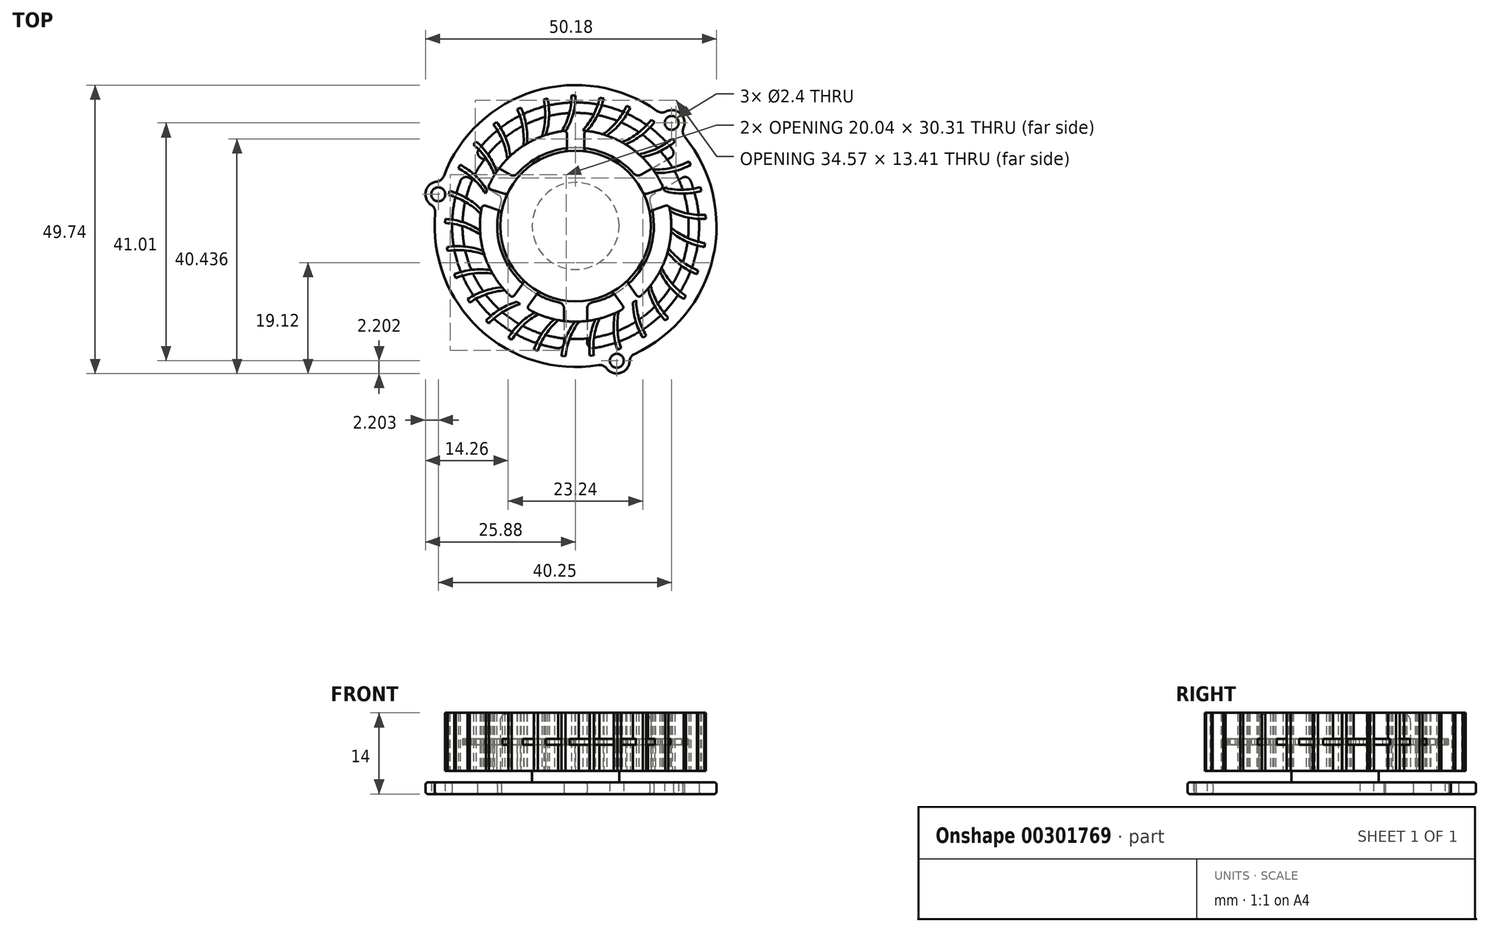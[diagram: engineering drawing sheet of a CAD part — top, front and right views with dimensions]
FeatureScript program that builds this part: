
annotation { "Feature Type Name" : "Feature", "Feature Type Description" : "" }
export const myFeature = defineFeature(function(context is Context, id is Id, definition is map)
    precondition{}
    {
        {
            var Q0;
            Q0=qCreatedBy(makeId("Top.planeOp"),FACE);
            var sketch = newSketch(context, id + "F0", { "sketchPlane" : qUnion([Q0])});
            skArc(sketch, "E0", {"start": v(-24.2, 2.23) * mm, "mid": v(-16.57, -17.77) * mm, "end": v(3.9, -23.98) * mm});
            skLineSegment(sketch, "E1", {"start": v(0, 0) * mm, "end": v(-18.45, 10.65) * mm, "construction": true});
            skLineSegment(sketch, "E2", {"start": v(18.45, 10.65) * mm, "end": v(0, 0) * mm, "construction": true});
            skLineSegment(sketch, "E3", {"start": v(0, 0) * mm, "end": v(0, -21.3) * mm, "construction": true});
            skLineSegment(sketch, "E4", {"start": v(-16.39, 11.77) * mm, "end": v(-11.29, 8.83) * mm});
            skLineSegment(sketch, "E5", {"start": v(11.29, 8.83) * mm, "end": v(16.39, 11.77) * mm});
            skLineSegment(sketch, "E6", {"start": v(-18.39, 8.3) * mm, "end": v(-13.29, 5.36) * mm});
            skLineSegment(sketch, "E7", {"start": v(-2, -14.19) * mm, "end": v(-2, -20.08) * mm});
            skLineSegment(sketch, "E8", {"start": v(18.39, 8.3) * mm, "end": v(13.29, 5.36) * mm});
            skLineSegment(sketch, "E9", {"start": v(2, -14.19) * mm, "end": v(2, -20.08) * mm});
            skCircle(sketch, "E10", {"center": v(0, 0) * mm, "radius": 2 * mm, "construction": true});
            skArc(sketch, "E11", {"start": v(-16.67, 13.26) * mm, "mid": v(-16.87, 12.45) * mm, "end": v(-16.39, 11.77) * mm});
            skArc(sketch, "E12", {"start": v(16.39, 11.77) * mm, "mid": v(16.87, 12.45) * mm, "end": v(16.67, 13.26) * mm});
            skArc(sketch, "E13", {"start": v(19.82, 7.8) * mm, "mid": v(19.22, 8.38) * mm, "end": v(18.39, 8.3) * mm});
            skArc(sketch, "E14", {"start": v(2, -20.08) * mm, "mid": v(2.35, -20.83) * mm, "end": v(3.15, -21.07) * mm});
            skArc(sketch, "E15", {"start": v(-3.15, -21.07) * mm, "mid": v(-2.35, -20.83) * mm, "end": v(-2, -20.08) * mm});
            skArc(sketch, "E16", {"start": v(-18.39, 8.3) * mm, "mid": v(-19.22, 8.38) * mm, "end": v(-19.82, 7.8) * mm});
            skArc(sketch, "E17.trimOffspring", {"start": v(-19.82, 7.8) * mm, "mid": v(-18.45, -10.65) * mm, "end": v(-3.15, -21.07) * mm});
            skArc(sketch, "E18.trimOffspring", {"start": v(3.15, -21.07) * mm, "mid": v(18.45, -10.65) * mm, "end": v(19.82, 7.8) * mm});
            skArc(sketch, "E19.trimOffspring", {"start": v(16.67, 13.26) * mm, "mid": v(0, 21.3) * mm, "end": v(-16.67, 13.26) * mm});
            skCircle(sketch, "E20", {"center": v(-23.68, 5.47) * mm, "radius": 1.2 * mm});
            skCircle(sketch, "E21", {"center": v(16.57, 17.77) * mm, "radius": 1.2 * mm});
            skCircle(sketch, "E22", {"center": v(7.1, -23.24) * mm, "radius": 1.2 * mm});
            skCircle(sketch, "E23", {"center": v(0, 0) * mm, "radius": 23.1 * mm, "construction": true});
            skArc(sketch, "E24", {"start": v(18.6, 16.91) * mm, "mid": v(18.07, 19.38) * mm, "end": v(15.57, 19.73) * mm});
            skArc(sketch, "E25", {"start": v(-23.94, 7.65) * mm, "mid": v(-25.82, 5.96) * mm, "end": v(-24.87, 3.62) * mm});
            skArc(sketch, "E26", {"start": v(5.35, -24.56) * mm, "mid": v(7.75, -25.34) * mm, "end": v(9.3, -23.35) * mm});
            skArc(sketch, "E27.trimOffspring", {"start": v(10.17, -22.07) * mm, "mid": v(23.68, -5.47) * mm, "end": v(18.82, 15.38) * mm});
            skArc(sketch, "E28.trimOffspring", {"start": v(14.03, 19.84) * mm, "mid": v(-7.1, 23.24) * mm, "end": v(-22.72, 8.6) * mm});
            skArc(sketch, "E29.filletArc", {"start": v(14.03, 19.84) * mm, "mid": v(14.78, 19.57) * mm, "end": v(15.57, 19.73) * mm});
            skArc(sketch, "E30.filletArc", {"start": v(18.6, 16.91) * mm, "mid": v(18.5, 16.11) * mm, "end": v(18.82, 15.38) * mm});
            skArc(sketch, "E31.filletArc", {"start": v(10.17, -22.07) * mm, "mid": v(9.56, -22.59) * mm, "end": v(9.3, -23.35) * mm});
            skArc(sketch, "E32.filletArc", {"start": v(5.35, -24.56) * mm, "mid": v(4.7, -24.07) * mm, "end": v(3.9, -23.98) * mm});
            skArc(sketch, "E33.filletArc", {"start": v(-24.2, 2.23) * mm, "mid": v(-24.34, 3.02) * mm, "end": v(-24.87, 3.62) * mm});
            skArc(sketch, "E34.filletArc", {"start": v(-23.94, 7.65) * mm, "mid": v(-23.2, 7.96) * mm, "end": v(-22.72, 8.6) * mm});
            skLineSegment(sketch, "E35", {"start": v(-23.68, 5.47) * mm, "end": v(0, 0) * mm, "construction": true});
            skLineSegment(sketch, "E36", {"start": v(0, 0) * mm, "end": v(16.57, 17.77) * mm, "construction": true});
            skArc(sketch, "E37", {"start": v(-12.83, 4.19) * mm, "mid": v(-11.7, -6.75) * mm, "end": v(-2.8, -13.2) * mm});
            skLineSegment(sketch, "E38.trimOffspring", {"start": v(0, 0) * mm, "end": v(7.1, -23.24) * mm, "construction": true});
            skArc(sketch, "E39.trimOffspring", {"start": v(10.04, 9.02) * mm, "mid": v(0, 13.5) * mm, "end": v(-10.04, 9.02) * mm});
            skArc(sketch, "E40.trimOffspring", {"start": v(2.8, -13.2) * mm, "mid": v(11.7, -6.75) * mm, "end": v(12.83, 4.19) * mm});
            skArc(sketch, "E41.filletArc", {"start": v(-11.29, 8.83) * mm, "mid": v(-10.63, 8.7) * mm, "end": v(-10.04, 9.02) * mm});
            skArc(sketch, "E42.filletArc", {"start": v(10.04, 9.02) * mm, "mid": v(10.63, 8.7) * mm, "end": v(11.29, 8.83) * mm});
            skArc(sketch, "E43.filletArc", {"start": v(13.29, 5.36) * mm, "mid": v(12.85, 4.85) * mm, "end": v(12.83, 4.19) * mm});
            skArc(sketch, "E44.filletArc", {"start": v(2.8, -13.2) * mm, "mid": v(2.22, -13.56) * mm, "end": v(2, -14.19) * mm});
            skArc(sketch, "E45.filletArc", {"start": v(-2, -14.19) * mm, "mid": v(-2.22, -13.56) * mm, "end": v(-2.8, -13.2) * mm});
            skArc(sketch, "E46.filletArc", {"start": v(-12.83, 4.19) * mm, "mid": v(-12.85, 4.85) * mm, "end": v(-13.29, 5.36) * mm});
            skCircle(sketch, "E47", {"center": v(0, 0) * mm, "radius": 7.5 * mm});
            skSolve(sketch);
        }
        {
            var Q0;
            Q0=makeQuery(id+"F0.imprint","IMPRINT",FACE,{"disambiguationData":[TD([[makeQuery(id+"F0.imprint","IMPRINT",EDGE,{"derivedFrom":sQuery(id+"F0.wireOp",EDGE,"E0")}),1.0]])]});
            var Q1;
            Q1=makeQuery(id+"F0.imprint","IMPRINT",FACE,{"disambiguationData":[TD([[makeQuery(id+"F0.imprint","IMPRINT",EDGE,{"derivedFrom":sQuery(id+"F0.wireOp",EDGE,"E47")}),1.0]])]});
            extrude(context, id + "F1", {"entities" : qUnion([Q0, Q1]), "depth" : 2 * mm});
        }
        {
            var Q0;
            Q0=makeQuery(id+"F1.opExtrude","CAP_EDGE",EDGE,{"disambiguationData":[OSD([sQuery(id+"F0.wireOp",EDGE,"E28.trimOffspring")])],"isStart":true});
            var Q1;
            Q1=makeQuery(id+"F1.opExtrude","CAP_EDGE",EDGE,{"disambiguationData":[OSD([sQuery(id+"F0.wireOp",EDGE,"E28.trimOffspring")])],"isStart":false});
            var Q2;
            Q2=makeQuery(id+"F1.opExtrude","CAP_EDGE",EDGE,{"disambiguationData":[OSD([sQuery(id+"F0.wireOp",EDGE,"E39.trimOffspring")])],"isStart":true});
            var Q3;
            Q3=makeQuery(id+"F1.opExtrude","CAP_EDGE",EDGE,{"disambiguationData":[OSD([sQuery(id+"F0.wireOp",EDGE,"E39.trimOffspring")])],"isStart":false});
            var Q4;
            Q4=makeQuery(id+"F1.opExtrude","CAP_EDGE",EDGE,{"disambiguationData":[OSD([sQuery(id+"F0.wireOp",EDGE,"E37")])],"isStart":true});
            var Q5;
            Q5=makeQuery(id+"F1.opExtrude","CAP_EDGE",EDGE,{"disambiguationData":[OSD([sQuery(id+"F0.wireOp",EDGE,"E37")])],"isStart":false});
            var Q6;
            Q6=makeQuery(id+"F1.opExtrude","CAP_EDGE",EDGE,{"disambiguationData":[OSD([sQuery(id+"F0.wireOp",EDGE,"E40.trimOffspring")])],"isStart":false});
            var Q7;
            Q7=makeQuery(id+"F1.opExtrude","CAP_EDGE",EDGE,{"disambiguationData":[OSD([sQuery(id+"F0.wireOp",EDGE,"E18.trimOffspring")])],"isStart":true});
            fillet(context, id + "F2", {"entities" : qUnion([Q0, Q1, Q2, Q3, Q4, Q5, Q6, Q7]), "radius" : 0.4 * mm, "tangentPropagation" : true, "allowEdgeOverflow" : false});
        }
        {
            var Q0;
            Q0=makeQuery(id+"F0.imprint","IMPRINT",FACE,{"disambiguationData":[TD([[makeQuery(id+"F0.imprint","IMPRINT",EDGE,{"derivedFrom":sQuery(id+"F0.wireOp",EDGE,"E47")}),1.0]])]});
            extrude(context, id + "F3", {"entities" : qUnion([Q0]), "operationType" : NewBodyOperationType.ADD, "depth" : 4 * mm});
        }
        {
            var Q0;
            Q0=makeQuery(id+"F3.opExtrude","CAP_FACE",FACE,{"disambiguationData":[OSD([sQuery(id+"F0.wireOp",EDGE,"E47")])],"isStart":false});
            var sketch = newSketch(context, id + "F4", { "sketchPlane" : qUnion([Q0])});
            skCircle(sketch, "E48", {"center": v(0, 0) * mm, "radius": 22.5 * mm, "construction": true});
            skCircle(sketch, "E49", {"center": v(0, 0) * mm, "radius": 19.5 * mm});
            skArc(sketch, "E50", {"start": v(-2.06, 16.37) * mm, "mid": v(-9.7, 13.35) * mm, "end": v(-14.93, 7.02) * mm});
            skArc(sketch, "E51", {"start": v(-1.93, 12.86) * mm, "mid": v(-7.64, 10.52) * mm, "end": v(-11.63, 5.8) * mm});
            skLineSegment(sketch, "E52", {"start": v(0, 13) * mm, "end": v(0, 16.5) * mm, "construction": true});
            skLineSegment(sketch, "E53", {"start": v(-1.5, 15.87) * mm, "end": v(-1.5, 13.35) * mm});
            skLineSegment(sketch, "E54", {"start": v(1.5, 15.87) * mm, "end": v(1.5, 13.35) * mm});
            skArc(sketch, "E55", {"start": v(-1.5, 15.87) * mm, "mid": v(-1.67, 16.25) * mm, "end": v(-2.06, 16.37) * mm});
            skArc(sketch, "E56", {"start": v(-1.93, 12.86) * mm, "mid": v(-1.62, 13.02) * mm, "end": v(-1.5, 13.35) * mm});
            skArc(sketch, "E57", {"start": v(1.5, 13.35) * mm, "mid": v(1.62, 13.02) * mm, "end": v(1.93, 12.86) * mm});
            skArc(sketch, "E58", {"start": v(2.06, 16.37) * mm, "mid": v(1.67, 16.25) * mm, "end": v(1.5, 15.87) * mm});
            skLineSegment(sketch, "E59.1.0", {"start": v(-12.36, 4.02) * mm, "end": v(-15.7, 5.1) * mm, "construction": true});
            skLineSegment(sketch, "E59.1.1", {"start": v(-14.63, 6.33) * mm, "end": v(-12.23, 5.55) * mm});
            skLineSegment(sketch, "E59.1.2", {"start": v(-15.56, 3.48) * mm, "end": v(-13.16, 2.7) * mm});
            skArc(sketch, "E59.1.3", {"start": v(-15.56, 3.48) * mm, "mid": v(-15.97, 3.43) * mm, "end": v(-16.2, 3.1) * mm});
            skArc(sketch, "E59.1.4", {"start": v(-12.82, 2.14) * mm, "mid": v(-12.89, 2.48) * mm, "end": v(-13.16, 2.7) * mm});
            skArc(sketch, "E59.1.5", {"start": v(-12.23, 5.55) * mm, "mid": v(-11.89, 5.57) * mm, "end": v(-11.63, 5.8) * mm});
            skArc(sketch, "E59.1.6", {"start": v(-14.93, 7.02) * mm, "mid": v(-14.94, 6.6) * mm, "end": v(-14.63, 6.33) * mm});
            skLineSegment(sketch, "E59.2.0", {"start": v(-7.64, -10.52) * mm, "end": v(-9.7, -13.35) * mm, "construction": true});
            skLineSegment(sketch, "E59.2.1", {"start": v(-10.54, -11.96) * mm, "end": v(-9.06, -9.92) * mm});
            skLineSegment(sketch, "E59.2.2", {"start": v(-8.12, -13.72) * mm, "end": v(-6.63, -11.68) * mm});
            skArc(sketch, "E59.2.3", {"start": v(-8.12, -13.72) * mm, "mid": v(-8.2, -14.13) * mm, "end": v(-7.95, -14.46) * mm});
            skArc(sketch, "E59.2.4", {"start": v(-6, -11.53) * mm, "mid": v(-6.34, -11.5) * mm, "end": v(-6.63, -11.68) * mm});
            skArc(sketch, "E59.2.5", {"start": v(-9.06, -9.92) * mm, "mid": v(-8.97, -9.58) * mm, "end": v(-9.11, -9.27) * mm});
            skArc(sketch, "E59.2.6", {"start": v(-11.3, -12.03) * mm, "mid": v(-10.9, -12.16) * mm, "end": v(-10.54, -11.96) * mm});
            skLineSegment(sketch, "E59.3.0", {"start": v(7.64, -10.52) * mm, "end": v(9.7, -13.35) * mm, "construction": true});
            skLineSegment(sketch, "E59.3.1", {"start": v(8.12, -13.72) * mm, "end": v(6.63, -11.68) * mm});
            skLineSegment(sketch, "E59.3.2", {"start": v(10.54, -11.96) * mm, "end": v(9.06, -9.92) * mm});
            skArc(sketch, "E59.3.3", {"start": v(10.54, -11.96) * mm, "mid": v(10.9, -12.16) * mm, "end": v(11.3, -12.03) * mm});
            skArc(sketch, "E59.3.4", {"start": v(9.11, -9.27) * mm, "mid": v(8.97, -9.58) * mm, "end": v(9.06, -9.92) * mm});
            skArc(sketch, "E59.3.5", {"start": v(6.63, -11.68) * mm, "mid": v(6.34, -11.5) * mm, "end": v(6, -11.53) * mm});
            skArc(sketch, "E59.3.6", {"start": v(7.95, -14.46) * mm, "mid": v(8.2, -14.13) * mm, "end": v(8.12, -13.72) * mm});
            skLineSegment(sketch, "E59.4.0", {"start": v(12.36, 4.02) * mm, "end": v(15.7, 5.1) * mm, "construction": true});
            skLineSegment(sketch, "E59.4.1", {"start": v(15.56, 3.48) * mm, "end": v(13.16, 2.7) * mm});
            skLineSegment(sketch, "E59.4.2", {"start": v(14.63, 6.33) * mm, "end": v(12.23, 5.55) * mm});
            skArc(sketch, "E59.4.3", {"start": v(14.63, 6.33) * mm, "mid": v(14.94, 6.6) * mm, "end": v(14.93, 7.02) * mm});
            skArc(sketch, "E59.4.4", {"start": v(11.63, 5.8) * mm, "mid": v(11.89, 5.57) * mm, "end": v(12.23, 5.55) * mm});
            skArc(sketch, "E59.4.5", {"start": v(13.16, 2.7) * mm, "mid": v(12.89, 2.48) * mm, "end": v(12.82, 2.14) * mm});
            skArc(sketch, "E59.4.6", {"start": v(16.2, 3.1) * mm, "mid": v(15.97, 3.43) * mm, "end": v(15.56, 3.48) * mm});
            skArc(sketch, "E60.trimOffspring", {"start": v(-16.2, 3.1) * mm, "mid": v(-15.7, -5.1) * mm, "end": v(-11.3, -12.03) * mm});
            skArc(sketch, "E61.trimOffspring", {"start": v(-12.82, 2.14) * mm, "mid": v(-12.36, -4.02) * mm, "end": v(-9.11, -9.27) * mm});
            skArc(sketch, "E62.trimOffspring", {"start": v(-6, -11.53) * mm, "mid": v(0, -13) * mm, "end": v(6, -11.53) * mm});
            skArc(sketch, "E63.trimOffspring", {"start": v(-7.95, -14.46) * mm, "mid": v(0, -16.5) * mm, "end": v(7.95, -14.46) * mm});
            skArc(sketch, "E64.trimOffspring", {"start": v(11.3, -12.03) * mm, "mid": v(15.7, -5.1) * mm, "end": v(16.2, 3.1) * mm});
            skArc(sketch, "E65.trimOffspring", {"start": v(9.11, -9.27) * mm, "mid": v(12.36, -4.02) * mm, "end": v(12.82, 2.14) * mm});
            skArc(sketch, "E66.trimOffspring", {"start": v(11.63, 5.8) * mm, "mid": v(7.64, 10.52) * mm, "end": v(1.93, 12.86) * mm});
            skArc(sketch, "E67.trimOffspring", {"start": v(14.93, 7.02) * mm, "mid": v(9.7, 13.35) * mm, "end": v(2.06, 16.37) * mm});
            skArc(sketch, "E68", {"start": v(-11.63, 5.8) * mm, "mid": v(-12.36, 4.02) * mm, "end": v(-12.82, 2.14) * mm});
            skArc(sketch, "E69", {"start": v(1.93, 12.86) * mm, "mid": v(0, 13) * mm, "end": v(-1.93, 12.86) * mm});
            skArc(sketch, "E70", {"start": v(12.82, 2.14) * mm, "mid": v(12.36, 4.02) * mm, "end": v(11.63, 5.8) * mm});
            skArc(sketch, "E71", {"start": v(6, -11.53) * mm, "mid": v(7.64, -10.52) * mm, "end": v(9.11, -9.27) * mm});
            skArc(sketch, "E72", {"start": v(-9.11, -9.27) * mm, "mid": v(-7.64, -10.52) * mm, "end": v(-6, -11.53) * mm});
            skSolve(sketch);
        }
        {
            var Q0;
            Q0=makeQuery(id+"F3.opExtrude","CAP_FACE",FACE,{"disambiguationData":[OSD([sQuery(id+"F0.wireOp",EDGE,"E47")])],"isStart":false});
            var sketch = newSketch(context, id + "F5", { "sketchPlane" : qUnion([Q0])});
            skLineSegment(sketch, "E73", {"start": v(0, 0) * mm, "end": v(0, 22.5) * mm, "construction": true});
            skLineSegment(sketch, "E74", {"start": v(-0.7, 22.49) * mm, "end": v(-0.7, 19.49) * mm, "construction": true});
            skLineSegment(sketch, "E75", {"start": v(-0.7, 22.49) * mm, "end": v(0, 22.5) * mm});
            skArc(sketch, "E76", {"start": v(-1.65, 16.42) * mm, "mid": v(-0.42, 19.35) * mm, "end": v(0, 22.5) * mm});
            skLineSegment(sketch, "E77", {"start": v(-1.65, 16.42) * mm, "end": v(-2.35, 16.33) * mm});
            skArc(sketch, "E78", {"start": v(-2.35, 16.33) * mm, "mid": v(-1.12, 19.3) * mm, "end": v(-0.7, 22.49) * mm});
            skLineSegment(sketch, "E79", {"start": v(-2.35, 16.33) * mm, "end": v(-0.7, 22.49) * mm, "construction": true});
            skLineSegment(sketch, "E80", {"start": v(-1.2, 16.46) * mm, "end": v(0.42, 22.5) * mm, "construction": true});
            skArc(sketch, "E81.1.0", {"start": v(-5.8, 15.44) * mm, "mid": v(-5.24, 18.6) * mm, "end": v(-5.52, 21.81) * mm});
            skLineSegment(sketch, "E81.1.1", {"start": v(-5.52, 21.81) * mm, "end": v(-4.84, 21.97) * mm});
            skArc(sketch, "E81.1.2", {"start": v(-5.15, 15.68) * mm, "mid": v(-4.57, 18.8) * mm, "end": v(-4.84, 21.97) * mm});
            skLineSegment(sketch, "E81.1.3", {"start": v(-5.15, 15.68) * mm, "end": v(-5.8, 15.44) * mm});
            skArc(sketch, "E81.2.0", {"start": v(-9, 13.84) * mm, "mid": v(-9.12, 17.05) * mm, "end": v(-10.08, 20.12) * mm});
            skLineSegment(sketch, "E81.2.1", {"start": v(-10.08, 20.12) * mm, "end": v(-9.45, 20.42) * mm});
            skArc(sketch, "E81.2.2", {"start": v(-8.4, 14.2) * mm, "mid": v(-8.5, 17.38) * mm, "end": v(-9.45, 20.42) * mm});
            skLineSegment(sketch, "E81.2.3", {"start": v(-8.4, 14.2) * mm, "end": v(-9, 13.84) * mm});
            skArc(sketch, "E81.3.0", {"start": v(-11.75, 11.58) * mm, "mid": v(-12.57, 14.69) * mm, "end": v(-14.17, 17.48) * mm});
            skLineSegment(sketch, "E81.3.1", {"start": v(-14.17, 17.48) * mm, "end": v(-13.62, 17.91) * mm});
            skArc(sketch, "E81.3.2", {"start": v(-11.25, 12.07) * mm, "mid": v(-12.04, 15.15) * mm, "end": v(-13.62, 17.91) * mm});
            skLineSegment(sketch, "E81.3.3", {"start": v(-11.25, 12.07) * mm, "end": v(-11.75, 11.58) * mm});
            skArc(sketch, "E81.4.0", {"start": v(-13.97, 8.78) * mm, "mid": v(-15.44, 11.64) * mm, "end": v(-17.6, 14.03) * mm});
            skLineSegment(sketch, "E81.4.1", {"start": v(-17.6, 14.03) * mm, "end": v(-17.15, 14.57) * mm});
            skArc(sketch, "E81.4.2", {"start": v(-13.58, 9.37) * mm, "mid": v(-15.02, 12.2) * mm, "end": v(-17.15, 14.57) * mm});
            skLineSegment(sketch, "E81.4.3", {"start": v(-13.58, 9.37) * mm, "end": v(-13.97, 8.78) * mm});
            skArc(sketch, "E81.5.0", {"start": v(-15.53, 5.57) * mm, "mid": v(-17.58, 8.05) * mm, "end": v(-20.2, 9.92) * mm});
            skLineSegment(sketch, "E81.5.1", {"start": v(-20.2, 9.92) * mm, "end": v(-19.88, 10.54) * mm});
            skArc(sketch, "E81.5.2", {"start": v(-15.28, 6.23) * mm, "mid": v(-17.3, 8.7) * mm, "end": v(-19.88, 10.54) * mm});
            skLineSegment(sketch, "E81.5.3", {"start": v(-15.28, 6.23) * mm, "end": v(-15.53, 5.57) * mm});
            skArc(sketch, "E81.6.0", {"start": v(-16.37, 2.1) * mm, "mid": v(-18.9, 4.09) * mm, "end": v(-21.86, 5.34) * mm});
            skLineSegment(sketch, "E81.6.1", {"start": v(-21.86, 5.34) * mm, "end": v(-21.68, 6.02) * mm});
            skArc(sketch, "E81.6.2", {"start": v(-16.26, 2.8) * mm, "mid": v(-18.76, 4.77) * mm, "end": v(-21.68, 6.02) * mm});
            skLineSegment(sketch, "E81.6.3", {"start": v(-16.26, 2.8) * mm, "end": v(-16.37, 2.1) * mm});
            skArc(sketch, "E81.7.0", {"start": v(-16.44, -1.46) * mm, "mid": v(-19.33, -0.07) * mm, "end": v(-22.5, 0.52) * mm});
            skLineSegment(sketch, "E81.7.1", {"start": v(-22.5, 0.52) * mm, "end": v(-22.47, 1.22) * mm});
            skArc(sketch, "E81.7.2", {"start": v(-16.48, -0.76) * mm, "mid": v(-19.34, 0.63) * mm, "end": v(-22.47, 1.22) * mm});
            skLineSegment(sketch, "E81.7.3", {"start": v(-16.48, -0.76) * mm, "end": v(-16.44, -1.46) * mm});
            skArc(sketch, "E81.8.0", {"start": v(-15.74, -4.96) * mm, "mid": v(-18.87, -4.23) * mm, "end": v(-22.08, -4.33) * mm});
            skLineSegment(sketch, "E81.8.1", {"start": v(-22.08, -4.33) * mm, "end": v(-22.2, -3.64) * mm});
            skArc(sketch, "E81.8.2", {"start": v(-15.93, -4.29) * mm, "mid": v(-19.02, -3.55) * mm, "end": v(-22.2, -3.64) * mm});
            skLineSegment(sketch, "E81.8.3", {"start": v(-15.93, -4.29) * mm, "end": v(-15.74, -4.96) * mm});
            skArc(sketch, "E81.9.0", {"start": v(-14.3, -8.23) * mm, "mid": v(-17.52, -8.18) * mm, "end": v(-20.63, -8.97) * mm});
            skLineSegment(sketch, "E81.9.1", {"start": v(-20.63, -8.97) * mm, "end": v(-20.9, -8.33) * mm});
            skArc(sketch, "E81.9.2", {"start": v(-14.64, -7.61) * mm, "mid": v(-17.82, -7.55) * mm, "end": v(-20.9, -8.33) * mm});
            skLineSegment(sketch, "E81.9.3", {"start": v(-14.64, -7.61) * mm, "end": v(-14.3, -8.23) * mm});
            skArc(sketch, "E81.10.0", {"start": v(-12.2, -11.11) * mm, "mid": v(-15.35, -11.76) * mm, "end": v(-18.22, -13.2) * mm});
            skLineSegment(sketch, "E81.10.1", {"start": v(-18.22, -13.2) * mm, "end": v(-18.62, -12.63) * mm});
            skArc(sketch, "E81.10.2", {"start": v(-12.66, -10.58) * mm, "mid": v(-15.78, -11.2) * mm, "end": v(-18.62, -12.63) * mm});
            skLineSegment(sketch, "E81.10.3", {"start": v(-12.66, -10.58) * mm, "end": v(-12.2, -11.11) * mm});
            skArc(sketch, "E81.11.0", {"start": v(-9.53, -13.47) * mm, "mid": v(-12.46, -14.78) * mm, "end": v(-14.96, -16.8) * mm});
            skLineSegment(sketch, "E81.11.1", {"start": v(-14.96, -16.8) * mm, "end": v(-15.47, -16.33) * mm});
            skArc(sketch, "E81.11.2", {"start": v(-10.09, -13.06) * mm, "mid": v(-13, -14.34) * mm, "end": v(-15.47, -16.33) * mm});
            skLineSegment(sketch, "E81.11.3", {"start": v(-10.09, -13.06) * mm, "end": v(-9.53, -13.47) * mm});
            skArc(sketch, "E81.12.0", {"start": v(-6.4, -15.2) * mm, "mid": v(-9, -17.12) * mm, "end": v(-11, -19.63) * mm});
            skLineSegment(sketch, "E81.12.1", {"start": v(-11, -19.63) * mm, "end": v(-11.6, -19.28) * mm});
            skArc(sketch, "E81.12.2", {"start": v(-7.05, -14.92) * mm, "mid": v(-9.61, -16.8) * mm, "end": v(-11.6, -19.28) * mm});
            skLineSegment(sketch, "E81.12.3", {"start": v(-7.05, -14.92) * mm, "end": v(-6.4, -15.2) * mm});
            skArc(sketch, "E81.13.0", {"start": v(-2.99, -16.23) * mm, "mid": v(-5.1, -18.65) * mm, "end": v(-6.52, -21.54) * mm});
            skLineSegment(sketch, "E81.13.1", {"start": v(-6.52, -21.54) * mm, "end": v(-7.18, -21.32) * mm});
            skArc(sketch, "E81.13.2", {"start": v(-3.67, -16.09) * mm, "mid": v(-5.78, -18.47) * mm, "end": v(-7.18, -21.32) * mm});
            skLineSegment(sketch, "E81.13.3", {"start": v(-3.67, -16.09) * mm, "end": v(-2.99, -16.23) * mm});
            skArc(sketch, "E81.14.0", {"start": v(0.57, -16.5) * mm, "mid": v(-0.97, -19.3) * mm, "end": v(-1.74, -22.43) * mm});
            skLineSegment(sketch, "E81.14.1", {"start": v(-1.74, -22.43) * mm, "end": v(-2.43, -22.37) * mm});
            skArc(sketch, "E81.14.2", {"start": v(-0.13, -16.5) * mm, "mid": v(-1.67, -19.28) * mm, "end": v(-2.43, -22.37) * mm});
            skLineSegment(sketch, "E81.14.3", {"start": v(-0.13, -16.5) * mm, "end": v(0.57, -16.5) * mm});
            skArc(sketch, "E81.15.0", {"start": v(4.1, -15.98) * mm, "mid": v(3.2, -19.07) * mm, "end": v(3.13, -22.28) * mm});
            skLineSegment(sketch, "E81.15.1", {"start": v(3.13, -22.28) * mm, "end": v(2.43, -22.37) * mm});
            skArc(sketch, "E81.15.2", {"start": v(3.42, -16.14) * mm, "mid": v(2.51, -19.19) * mm, "end": v(2.43, -22.37) * mm});
            skLineSegment(sketch, "E81.15.3", {"start": v(3.42, -16.14) * mm, "end": v(4.1, -15.98) * mm});
            skArc(sketch, "E81.16.0", {"start": v(7.44, -14.73) * mm, "mid": v(7.22, -17.93) * mm, "end": v(7.84, -21.09) * mm});
            skLineSegment(sketch, "E81.16.1", {"start": v(7.84, -21.09) * mm, "end": v(7.18, -21.32) * mm});
            skArc(sketch, "E81.16.2", {"start": v(6.81, -15.03) * mm, "mid": v(6.58, -18.2) * mm, "end": v(7.18, -21.32) * mm});
            skLineSegment(sketch, "E81.16.3", {"start": v(6.81, -15.03) * mm, "end": v(7.44, -14.73) * mm});
            skArc(sketch, "E81.17.0", {"start": v(10.43, -12.78) * mm, "mid": v(10.91, -15.96) * mm, "end": v(12.2, -18.9) * mm});
            skLineSegment(sketch, "E81.17.1", {"start": v(12.2, -18.9) * mm, "end": v(11.6, -19.28) * mm});
            skArc(sketch, "E81.17.2", {"start": v(9.88, -13.21) * mm, "mid": v(10.34, -16.36) * mm, "end": v(11.6, -19.28) * mm});
            skLineSegment(sketch, "E81.17.3", {"start": v(9.88, -13.21) * mm, "end": v(10.43, -12.78) * mm});
            skArc(sketch, "E81.18.0", {"start": v(12.94, -10.24) * mm, "mid": v(14.09, -13.24) * mm, "end": v(15.97, -15.85) * mm});
            skLineSegment(sketch, "E81.18.1", {"start": v(15.97, -15.85) * mm, "end": v(15.47, -16.33) * mm});
            skArc(sketch, "E81.18.2", {"start": v(12.5, -10.78) * mm, "mid": v(13.61, -13.76) * mm, "end": v(15.47, -16.33) * mm});
            skLineSegment(sketch, "E81.18.3", {"start": v(12.5, -10.78) * mm, "end": v(12.94, -10.24) * mm});
            skArc(sketch, "E81.19.0", {"start": v(14.84, -7.22) * mm, "mid": v(16.6, -9.9) * mm, "end": v(19, -12.04) * mm});
            skLineSegment(sketch, "E81.19.1", {"start": v(19, -12.04) * mm, "end": v(18.62, -12.63) * mm});
            skArc(sketch, "E81.19.2", {"start": v(14.52, -7.84) * mm, "mid": v(16.25, -10.5) * mm, "end": v(18.62, -12.63) * mm});
            skLineSegment(sketch, "E81.19.3", {"start": v(14.52, -7.84) * mm, "end": v(14.84, -7.22) * mm});
            skArc(sketch, "E81.20.0", {"start": v(16.04, -3.86) * mm, "mid": v(18.35, -6.1) * mm, "end": v(21.15, -7.67) * mm});
            skLineSegment(sketch, "E81.20.1", {"start": v(21.15, -7.67) * mm, "end": v(20.9, -8.33) * mm});
            skArc(sketch, "E81.20.2", {"start": v(15.86, -4.54) * mm, "mid": v(18.13, -6.77) * mm, "end": v(20.9, -8.33) * mm});
            skLineSegment(sketch, "E81.20.3", {"start": v(15.86, -4.54) * mm, "end": v(16.04, -3.86) * mm});
            skArc(sketch, "E81.21.0", {"start": v(16.5, -0.32) * mm, "mid": v(19.23, -2.02) * mm, "end": v(22.3, -2.95) * mm});
            skLineSegment(sketch, "E81.21.1", {"start": v(22.3, -2.95) * mm, "end": v(22.2, -3.64) * mm});
            skArc(sketch, "E81.21.2", {"start": v(16.47, -1.02) * mm, "mid": v(19.16, -2.71) * mm, "end": v(22.2, -3.64) * mm});
            skLineSegment(sketch, "E81.21.3", {"start": v(16.47, -1.02) * mm, "end": v(16.5, -0.32) * mm});
            skArc(sketch, "E81.22.0", {"start": v(16.18, 3.23) * mm, "mid": v(19.21, 2.16) * mm, "end": v(22.42, 1.92) * mm});
            skLineSegment(sketch, "E81.22.1", {"start": v(22.42, 1.92) * mm, "end": v(22.47, 1.22) * mm});
            skArc(sketch, "E81.22.2", {"start": v(16.3, 2.54) * mm, "mid": v(19.3, 1.47) * mm, "end": v(22.47, 1.22) * mm});
            skLineSegment(sketch, "E81.22.3", {"start": v(16.3, 2.54) * mm, "end": v(16.18, 3.23) * mm});
            skArc(sketch, "E81.23.0", {"start": v(15.1, 6.63) * mm, "mid": v(18.3, 6.24) * mm, "end": v(21.48, 6.7) * mm});
            skLineSegment(sketch, "E81.23.1", {"start": v(21.48, 6.7) * mm, "end": v(21.68, 6.02) * mm});
            skArc(sketch, "E81.23.2", {"start": v(15.38, 5.99) * mm, "mid": v(18.53, 5.58) * mm, "end": v(21.68, 6.02) * mm});
            skLineSegment(sketch, "E81.23.3", {"start": v(15.38, 5.99) * mm, "end": v(15.1, 6.63) * mm});
            skArc(sketch, "E81.24.0", {"start": v(13.33, 9.73) * mm, "mid": v(16.53, 10.03) * mm, "end": v(19.54, 11.15) * mm});
            skLineSegment(sketch, "E81.24.1", {"start": v(19.54, 11.15) * mm, "end": v(19.88, 10.54) * mm});
            skArc(sketch, "E81.24.2", {"start": v(13.73, 9.15) * mm, "mid": v(16.9, 9.43) * mm, "end": v(19.88, 10.54) * mm});
            skLineSegment(sketch, "E81.24.3", {"start": v(13.73, 9.15) * mm, "end": v(13.33, 9.73) * mm});
            skArc(sketch, "E81.25.0", {"start": v(10.93, 12.36) * mm, "mid": v(13.99, 13.35) * mm, "end": v(16.69, 15.1) * mm});
            skLineSegment(sketch, "E81.25.1", {"start": v(16.69, 15.1) * mm, "end": v(17.15, 14.57) * mm});
            skArc(sketch, "E81.25.2", {"start": v(11.44, 11.89) * mm, "mid": v(14.47, 12.85) * mm, "end": v(17.15, 14.57) * mm});
            skLineSegment(sketch, "E81.25.3", {"start": v(11.44, 11.89) * mm, "end": v(10.93, 12.36) * mm});
            skArc(sketch, "E81.26.0", {"start": v(8.01, 14.42) * mm, "mid": v(10.79, 16.04) * mm, "end": v(13.05, 18.33) * mm});
            skLineSegment(sketch, "E81.26.1", {"start": v(13.05, 18.33) * mm, "end": v(13.62, 17.91) * mm});
            skArc(sketch, "E81.26.2", {"start": v(8.62, 14.07) * mm, "mid": v(11.37, 15.66) * mm, "end": v(13.62, 17.91) * mm});
            skLineSegment(sketch, "E81.26.3", {"start": v(8.62, 14.07) * mm, "end": v(8.01, 14.42) * mm});
            skArc(sketch, "E81.27.0", {"start": v(4.72, 15.8) * mm, "mid": v(7.09, 17.99) * mm, "end": v(8.8, 20.7) * mm});
            skLineSegment(sketch, "E81.27.1", {"start": v(8.8, 20.7) * mm, "end": v(9.45, 20.42) * mm});
            skArc(sketch, "E81.27.2", {"start": v(5.4, 15.6) * mm, "mid": v(7.74, 17.74) * mm, "end": v(9.45, 20.42) * mm});
            skLineSegment(sketch, "E81.27.3", {"start": v(5.4, 15.6) * mm, "end": v(4.72, 15.8) * mm});
            skArc(sketch, "E81.28.0", {"start": v(1.22, 16.46) * mm, "mid": v(3.06, 19.1) * mm, "end": v(4.15, 22.11) * mm});
            skLineSegment(sketch, "E81.28.1", {"start": v(4.15, 22.11) * mm, "end": v(4.84, 21.97) * mm});
            skArc(sketch, "E81.28.2", {"start": v(1.91, 16.39) * mm, "mid": v(3.75, 18.99) * mm, "end": v(4.84, 21.97) * mm});
            skLineSegment(sketch, "E81.28.3", {"start": v(1.91, 16.39) * mm, "end": v(1.22, 16.46) * mm});
            skPoint(sketch, "E81.center", {"position": v(0, 0) * mm});
            skSolve(sketch);
        }
        {
            var Q0;
            Q0=makeQuery(id+"F4.imprint","IMPRINT",FACE,{"disambiguationData":[TD([[makeQuery(id+"F4.imprint","IMPRINT",EDGE,{"derivedFrom":sQuery(id+"F4.wireOp",EDGE,"E51")}),1.0]])]});
            var Q1;
            Q1=makeQuery(id+"F4.imprint","IMPRINT",FACE,{"disambiguationData":[TD([[makeQuery(id+"F4.imprint","IMPRINT",EDGE,{"derivedFrom":makeQuery(id+"F3.opExtrude","CAP_EDGE",EDGE,{"disambiguationData":[OSD([sQuery(id+"F0.wireOp",EDGE,"E47")])],"isStart":false})}),1.0]])]});
            extrude(context, id + "F6", {"entities" : qUnion([Q0, Q1]), "operationType" : NewBodyOperationType.ADD, "depth" : 10 * mm});
        }
        {
            var Q0;
            Q0=makeQuery(id+"F6.opExtrude","CAP_EDGE",EDGE,{"disambiguationData":[OSD([sQuery(id+"F4.wireOp",EDGE,"E51"),sQuery(id+"F4.wireOp",EDGE,"E61.trimOffspring"),sQuery(id+"F4.wireOp",EDGE,"E62.trimOffspring"),sQuery(id+"F4.wireOp",EDGE,"E65.trimOffspring"),sQuery(id+"F4.wireOp",EDGE,"E66.trimOffspring"),sQuery(id+"F4.wireOp",EDGE,"E68"),sQuery(id+"F4.wireOp",EDGE,"E69"),sQuery(id+"F4.wireOp",EDGE,"E70"),sQuery(id+"F4.wireOp",EDGE,"E71"),sQuery(id+"F4.wireOp",EDGE,"E72")])],"isStart":false});
            fillet(context, id + "F7", {"entities" : qUnion([Q0]), "radius" : 1.5 * mm, "tangentPropagation" : true, "allowEdgeOverflow" : false});
        }
        {
            var Q0;
            Q0=makeQuery(id+"F4.imprint","IMPRINT",FACE,{"disambiguationData":[TD([[makeQuery(id+"F4.imprint","IMPRINT",EDGE,{"derivedFrom":sQuery(id+"F4.wireOp",EDGE,"E49")}),1.0]])]});
            extrude(context, id + "F8", {"entities" : qUnion([Q0]), "operationType" : NewBodyOperationType.ADD, "depth" : 5.5 * mm, "hasSecondDirection" : true, "secondDirectionOppositeDirection" : false, "secondDirectionDepth" : 4.5 * mm});
        }
        {
            var Q0;
            Q0 = qSketchRegion(id + "F5", true);
            extrude(context, id + "F9", {"entities" : qUnion([Q0]), "operationType" : NewBodyOperationType.ADD, "depth" : 10 * mm});
        }
    });
